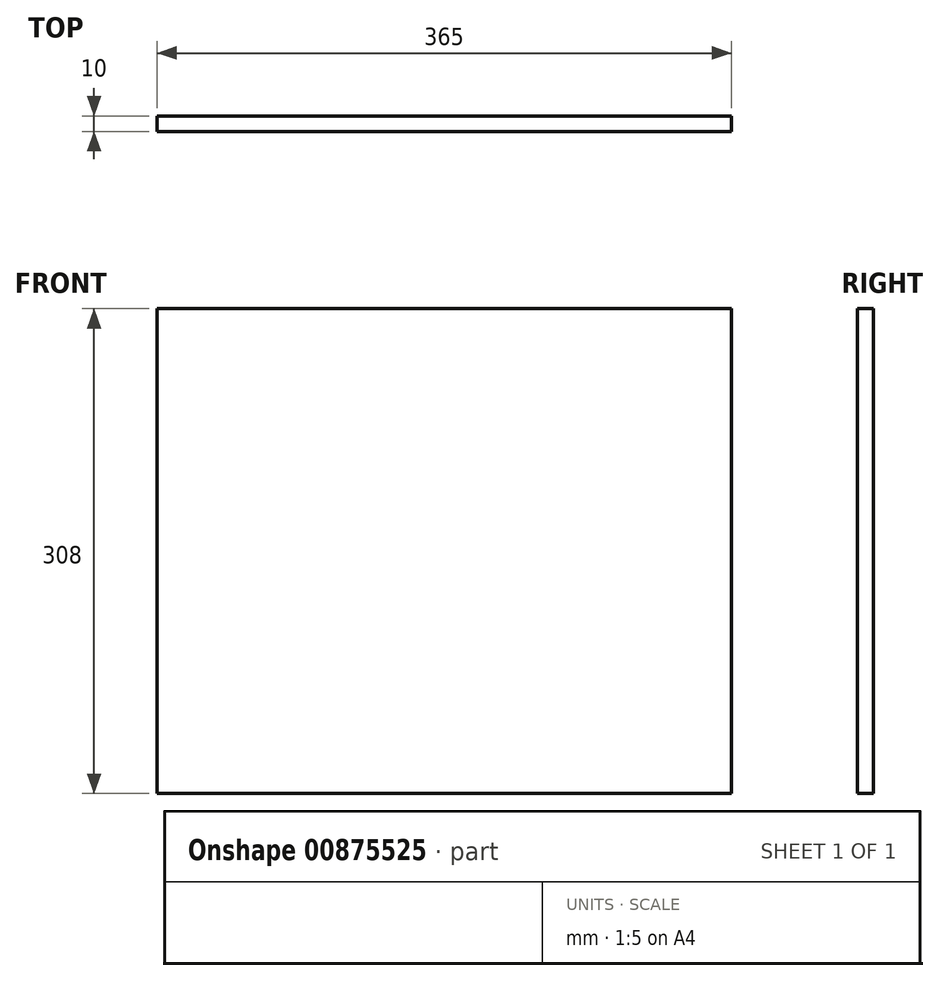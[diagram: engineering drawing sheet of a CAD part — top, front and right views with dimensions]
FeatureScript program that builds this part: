
annotation { "Feature Type Name" : "Feature", "Feature Type Description" : "" }
export const myFeature = defineFeature(function(context is Context, id is Id, definition is map)
    precondition{}
    {
        {
            var Q0;
            Q0=qCreatedBy(makeId("Front.planeOp"),FACE);
            var sketch = newSketch(context, id + "F0", { "sketchPlane" : qUnion([Q0])});
            skLineSegment(sketch, "E0.bottom", {"start": v(-4.86, 299.4) * mm, "end": v(360.14, 299.4) * mm});
            skLineSegment(sketch, "E0.top", {"start": v(-4.86, -8.6) * mm, "end": v(360.14, -8.6) * mm});
            skLineSegment(sketch, "E0.left", {"start": v(-4.86, 299.4) * mm, "end": v(-4.86, -8.6) * mm});
            skLineSegment(sketch, "E0.right", {"start": v(360.14, 299.4) * mm, "end": v(360.14, -8.6) * mm});
            skSolve(sketch);
        }
        {
            var Q0;
            Q0=makeQuery(id+"F0.imprint","IMPRINT",FACE,{"disambiguationData":[TD([[makeQuery(id+"F0.imprint","IMPRINT",EDGE,{"derivedFrom":sQuery(id+"F0.wireOp",EDGE,"E0.bottom")}),-1.0]])]});
            extrude(context, id + "F1", {"entities" : qUnion([Q0]), "depth" : 10 * mm, "offsetDistance" : 25 * mm});
        }
    });
